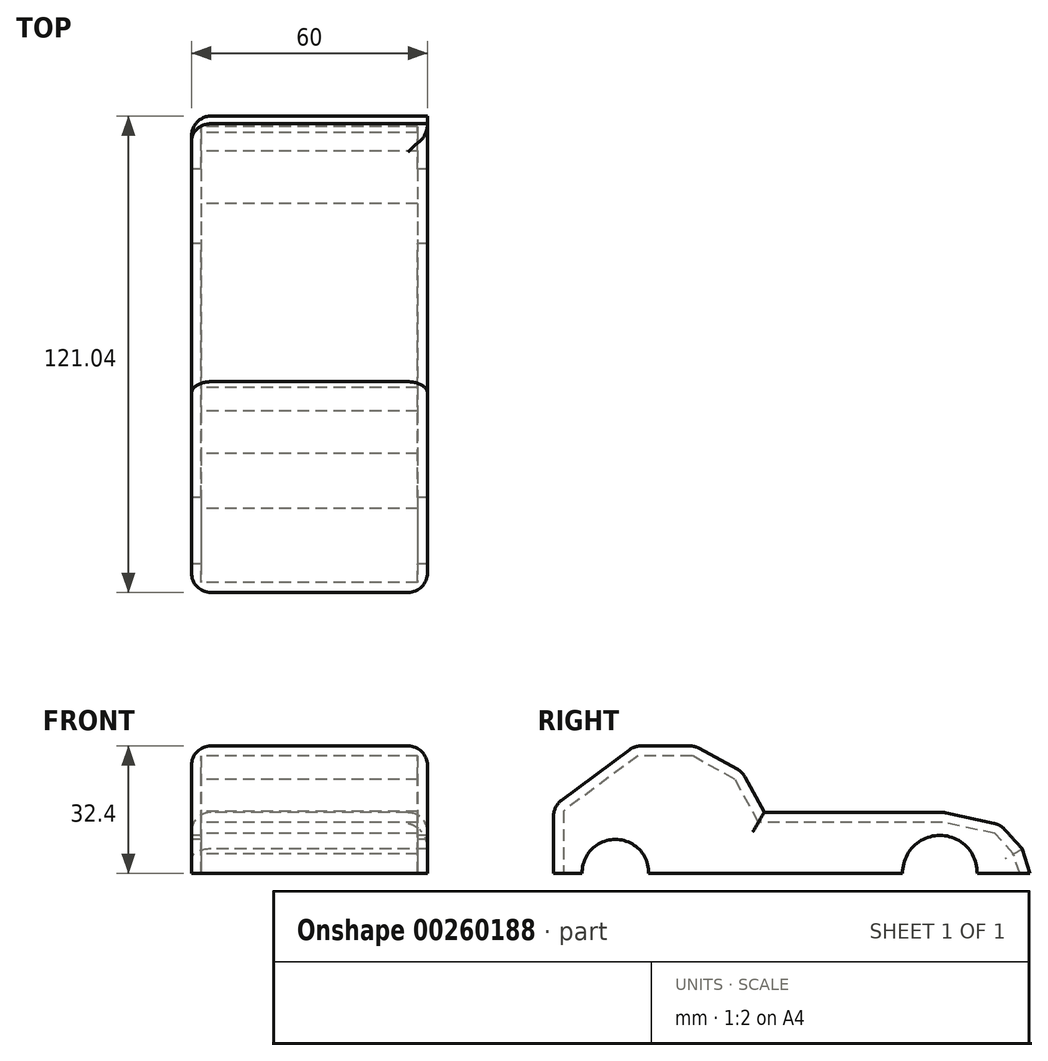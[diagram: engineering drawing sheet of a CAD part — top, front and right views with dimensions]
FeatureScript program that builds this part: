
annotation { "Feature Type Name" : "Feature", "Feature Type Description" : "" }
export const myFeature = defineFeature(function(context is Context, id is Id, definition is map)
    precondition{}
    {
        {
            var Q0;
            Q0=qCreatedBy(makeId("Right.planeOp"),FACE);
            var sketch = newSketch(context, id + "F0", { "sketchPlane" : qUnion([Q0])});
            skLineSegment(sketch, "E0", {"start": v(-65.37, 6.98) * mm, "end": v(-65.37, -10.09) * mm});
            skLineSegment(sketch, "E1", {"start": v(-65.37, -10.09) * mm, "end": v(55.67, -10.09) * mm});
            skLineSegment(sketch, "E2", {"start": v(55.67, -10.09) * mm, "end": v(53.73, -3.88) * mm});
            skLineSegment(sketch, "E3", {"start": v(53.73, -3.88) * mm, "end": v(48.1, 2.33) * mm});
            skLineSegment(sketch, "E4", {"start": v(48.1, 2.33) * mm, "end": v(33.75, 5.43) * mm});
            skLineSegment(sketch, "E5", {"start": v(33.75, 5.43) * mm, "end": v(20.56, 5.43) * mm});
            skLineSegment(sketch, "E6", {"start": v(20.56, 5.43) * mm, "end": v(4.46, 5.43) * mm});
            skLineSegment(sketch, "E7", {"start": v(4.46, 5.43) * mm, "end": v(-11.83, 5.43) * mm});
            skLineSegment(sketch, "E8", {"start": v(-11.83, 5.43) * mm, "end": v(-17.46, 15.71) * mm});
            skLineSegment(sketch, "E9", {"start": v(-17.46, 15.71) * mm, "end": v(-29.48, 22.3) * mm});
            skLineSegment(sketch, "E10", {"start": v(-29.48, 22.3) * mm, "end": v(-44.8, 22.3) * mm});
            skLineSegment(sketch, "E11", {"start": v(-44.8, 22.3) * mm, "end": v(-65.37, 6.98) * mm});
            skSolve(sketch);
        }
        {
            var Q0;
            Q0 = qSketchRegion(id + "F0", true);
            extrude(context, id + "F1", {"entities" : qUnion([Q0]), "depth" : 60 * mm});
        }
        {
            var Q0;
            Q0=makeQuery(id+"F1.opExtrude","SWEPT_FACE",FACE,{"disambiguationData":[OSD([sQuery(id+"F0.wireOp",EDGE,"E1")])]});
            shell(context, id + "F2", {"entities" : qUnion([Q0]), "thickness" : 2.5 * mm});
        }
        {
            var Q0;
            Q0=makeQuery(id+"F1.opExtrude","CAP_EDGE",EDGE,{"disambiguationData":[OSD([sQuery(id+"F0.wireOp",EDGE,"E2")])],"isStart":true});
            var Q1;
            Q1=makeQuery(id+"F1.opExtrude","CAP_EDGE",EDGE,{"disambiguationData":[OSD([sQuery(id+"F0.wireOp",EDGE,"E3")])],"isStart":true});
            var Q2;
            Q2=makeQuery(id+"F1.opExtrude","SWEPT_FACE",FACE,{"disambiguationData":[OSD([sQuery(id+"F0.wireOp",EDGE,"E4")])]});
            var Q3;
            Q3=makeQuery(id+"F1.opExtrude","CAP_EDGE",EDGE,{"disambiguationData":[OSD([sQuery(id+"F0.wireOp",EDGE,"E5"),sQuery(id+"F0.wireOp",EDGE,"E6"),sQuery(id+"F0.wireOp",EDGE,"E7")])],"isStart":true});
            var Q4;
            Q4=makeQuery(id+"F1.opExtrude","CAP_EDGE",EDGE,{"disambiguationData":[OSD([sQuery(id+"F0.wireOp",EDGE,"E8")])],"isStart":true});
            var Q5;
            Q5=makeQuery(id+"F1.opExtrude","CAP_EDGE",EDGE,{"disambiguationData":[OSD([sQuery(id+"F0.wireOp",EDGE,"E9")])],"isStart":true});
            var Q6;
            Q6=makeQuery(id+"F1.opExtrude","CAP_EDGE",EDGE,{"disambiguationData":[OSD([sQuery(id+"F0.wireOp",EDGE,"E10")])],"isStart":true});
            var Q7;
            Q7=makeQuery(id+"F1.opExtrude","CAP_EDGE",EDGE,{"disambiguationData":[OSD([sQuery(id+"F0.wireOp",EDGE,"E11")])],"isStart":true});
            var Q8;
            Q8=makeQuery(id+"F1.opExtrude","CAP_EDGE",EDGE,{"disambiguationData":[OSD([sQuery(id+"F0.wireOp",EDGE,"E0")])],"isStart":true});
            var Q9;
            Q9=makeQuery(id+"F1.opExtrude","CAP_EDGE",EDGE,{"disambiguationData":[OSD([sQuery(id+"F0.wireOp",EDGE,"E5"),sQuery(id+"F0.wireOp",EDGE,"E6"),sQuery(id+"F0.wireOp",EDGE,"E7")])],"isStart":false});
            var Q10;
            Q10=makeQuery(id+"F1.opExtrude","CAP_EDGE",EDGE,{"disambiguationData":[OSD([sQuery(id+"F0.wireOp",EDGE,"E8")])],"isStart":false});
            var Q11;
            Q11=makeQuery(id+"F1.opExtrude","CAP_EDGE",EDGE,{"disambiguationData":[OSD([sQuery(id+"F0.wireOp",EDGE,"E9")])],"isStart":false});
            var Q12;
            Q12=makeQuery(id+"F1.opExtrude","CAP_EDGE",EDGE,{"disambiguationData":[OSD([sQuery(id+"F0.wireOp",EDGE,"E10")])],"isStart":false});
            var Q13;
            Q13=makeQuery(id+"F1.opExtrude","CAP_EDGE",EDGE,{"disambiguationData":[OSD([sQuery(id+"F0.wireOp",EDGE,"E11")])],"isStart":false});
            var Q14;
            Q14=makeQuery(id+"F1.opExtrude","CAP_EDGE",EDGE,{"disambiguationData":[OSD([sQuery(id+"F0.wireOp",EDGE,"E0")])],"isStart":false});
            var Q15;
            Q15=makeQuery(id+"F1.opExtrude","SWEPT_FACE",FACE,{"disambiguationData":[OSD([sQuery(id+"F0.wireOp",EDGE,"E11")])]});
            var Q16;
            Q16=makeQuery(id+"F1.opExtrude","SWEPT_EDGE",EDGE,{"disambiguationData":[OSD([sQuery(id+"F0.wireOp",EDGE,"E10"),sQuery(id+"F0.wireOp",EDGE,"E11")])]});
            var Q17;
            Q17=makeQuery(id+"F1.opExtrude","SWEPT_EDGE",EDGE,{"disambiguationData":[OSD([sQuery(id+"F0.wireOp",EDGE,"E9"),sQuery(id+"F0.wireOp",EDGE,"E10")])]});
            var Q18;
            Q18=makeQuery(id+"F1.opExtrude","SWEPT_EDGE",EDGE,{"disambiguationData":[OSD([sQuery(id+"F0.wireOp",EDGE,"E8"),sQuery(id+"F0.wireOp",EDGE,"E9")])]});
            fillet(context, id + "F3", {"entities" : qUnion([Q0, Q1, Q2, Q3, Q4, Q5, Q6, Q7, Q8, Q9, Q10, Q11, Q12, Q13, Q14, Q15, Q16, Q17, Q18]), "radius" : 5 * mm, "tangentPropagation" : true, "allowEdgeOverflow" : false});
        }
        {
            var Q0;
            Q0=qCreatedBy(makeId("Right.planeOp"),FACE);
            var sketch = newSketch(context, id + "F4", { "sketchPlane" : qUnion([Q0])});
            skCircle(sketch, "E12", {"center": v(33.94, -9.9) * mm, "radius": 8.97 * mm});
            skCircle(sketch, "E13", {"center": v(-48.3, -9.7) * mm, "radius": 8.52 * mm});
            skSolve(sketch);
        }
        {
            var Q0;
            Q0=makeQuery(id+"F4.imprint","IMPRINT",FACE,{"disambiguationData":[TD([[makeQuery(id+"F4.imprint","IMPRINT",EDGE,{"derivedFrom":sQuery(id+"F4.wireOp",EDGE,"E12")}),1.0]])]});
            var Q1;
            Q1=makeQuery(id+"F4.imprint","IMPRINT",FACE,{"disambiguationData":[TD([[makeQuery(id+"F4.imprint","IMPRINT",EDGE,{"derivedFrom":sQuery(id+"F4.wireOp",EDGE,"E13")}),1.0]])]});
            extrude(context, id + "F5", {"entities" : qUnion([Q0, Q1]), "operationType" : NewBodyOperationType.REMOVE, "oppositeDirection" : true, "depth" : 60 * mm});
        }
        {
            var Q0;
            Q0=qCreatedBy(makeId("Right.planeOp"),FACE);
            var sketch = newSketch(context, id + "F6", { "sketchPlane" : qUnion([Q0])});
            skCircle(sketch, "E14", {"center": v(32.78, -9.9) * mm, "radius": 9.47 * mm});
            skCircle(sketch, "E15", {"center": v(-49.66, -9.9) * mm, "radius": 8.45 * mm});
            skSolve(sketch);
        }
        {
            var Q0;
            Q0 = qSketchRegion(id + "F6", true);
            extrude(context, id + "F7", {"entities" : qUnion([Q0]), "operationType" : NewBodyOperationType.REMOVE, "depth" : 65.4 * mm});
        }
    });
